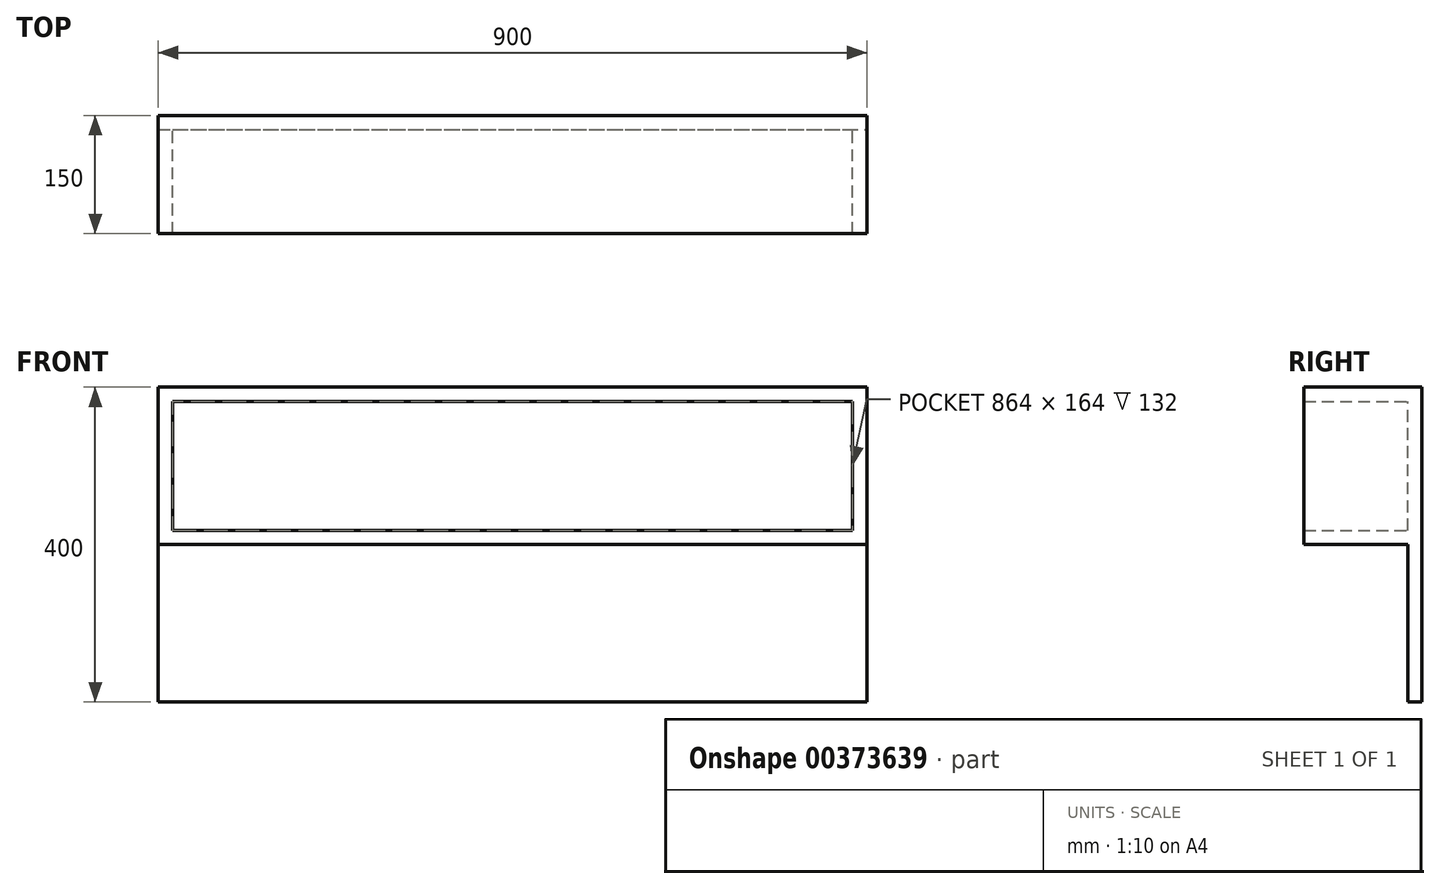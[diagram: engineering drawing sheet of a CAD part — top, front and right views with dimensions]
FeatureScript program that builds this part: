
annotation { "Feature Type Name" : "Feature", "Feature Type Description" : "" }
export const myFeature = defineFeature(function(context is Context, id is Id, definition is map)
    precondition{}
    {
        {
            var Q0;
            Q0=qCreatedBy(makeId("Front.planeOp"),FACE);
            var sketch = newSketch(context, id + "F0", { "sketchPlane" : qUnion([Q0])});
            skLineSegment(sketch, "E0", {"start": v(-138.25, 317.83) * mm, "end": v(761.75, 317.83) * mm});
            skLineSegment(sketch, "E1", {"start": v(761.75, -82.17) * mm, "end": v(-138.25, -82.17) * mm});
            skLineSegment(sketch, "E2", {"start": v(-138.25, 117.83) * mm, "end": v(761.75, 117.83) * mm});
            skLineSegment(sketch, "E3", {"start": v(-138.25, 117.83) * mm, "end": v(-138.25, 317.83) * mm});
            skLineSegment(sketch, "E4", {"start": v(761.75, 317.83) * mm, "end": v(761.75, 117.83) * mm});
            skLineSegment(sketch, "E5", {"start": v(761.75, -82.17) * mm, "end": v(761.75, 117.83) * mm});
            skLineSegment(sketch, "E6", {"start": v(-138.25, 117.83) * mm, "end": v(-138.25, -82.17) * mm});
            skLineSegment(sketch, "E7.0", {"start": v(-120.25, 299.83) * mm, "end": v(743.75, 299.83) * mm});
            skLineSegment(sketch, "E7.1", {"start": v(-120.25, 135.83) * mm, "end": v(-120.25, 299.83) * mm});
            skLineSegment(sketch, "E7.2", {"start": v(-120.25, 135.83) * mm, "end": v(743.75, 135.83) * mm});
            skLineSegment(sketch, "E7.3", {"start": v(743.75, 299.83) * mm, "end": v(743.75, 135.83) * mm});
            skSolve(sketch);
        }
        {
            var Q0;
            Q0=makeQuery(id+"F0.imprint","IMPRINT",FACE,{"disambiguationData":[TD([[makeQuery(id+"F0.imprint","IMPRINT",EDGE,{"derivedFrom":sQuery(id+"F0.wireOp",EDGE,"E0")}),-1.0]])]});
            extrude(context, id + "F1", {"entities" : qUnion([Q0]), "depth" : 150 * mm});
        }
        {
            var Q0;
            Q0=makeQuery(id+"F0.imprint","IMPRINT",FACE,{"disambiguationData":[TD([[makeQuery(id+"F0.imprint","IMPRINT",EDGE,{"derivedFrom":sQuery(id+"F0.wireOp",EDGE,"E1")}),-1.0]])]});
            extrude(context, id + "F2", {"entities" : qUnion([Q0]), "operationType" : NewBodyOperationType.ADD, "depth" : 18 * mm});
        }
        {
            var Q0;
            Q0=makeQuery(id+"F0.imprint","IMPRINT",FACE,{"disambiguationData":[TD([[makeQuery(id+"F0.imprint","IMPRINT",EDGE,{"derivedFrom":sQuery(id+"F0.wireOp",EDGE,"E7.0")}),-1.0]])]});
            extrude(context, id + "F3", {"entities" : qUnion([Q0]), "operationType" : NewBodyOperationType.ADD, "depth" : 18 * mm});
        }
    });
